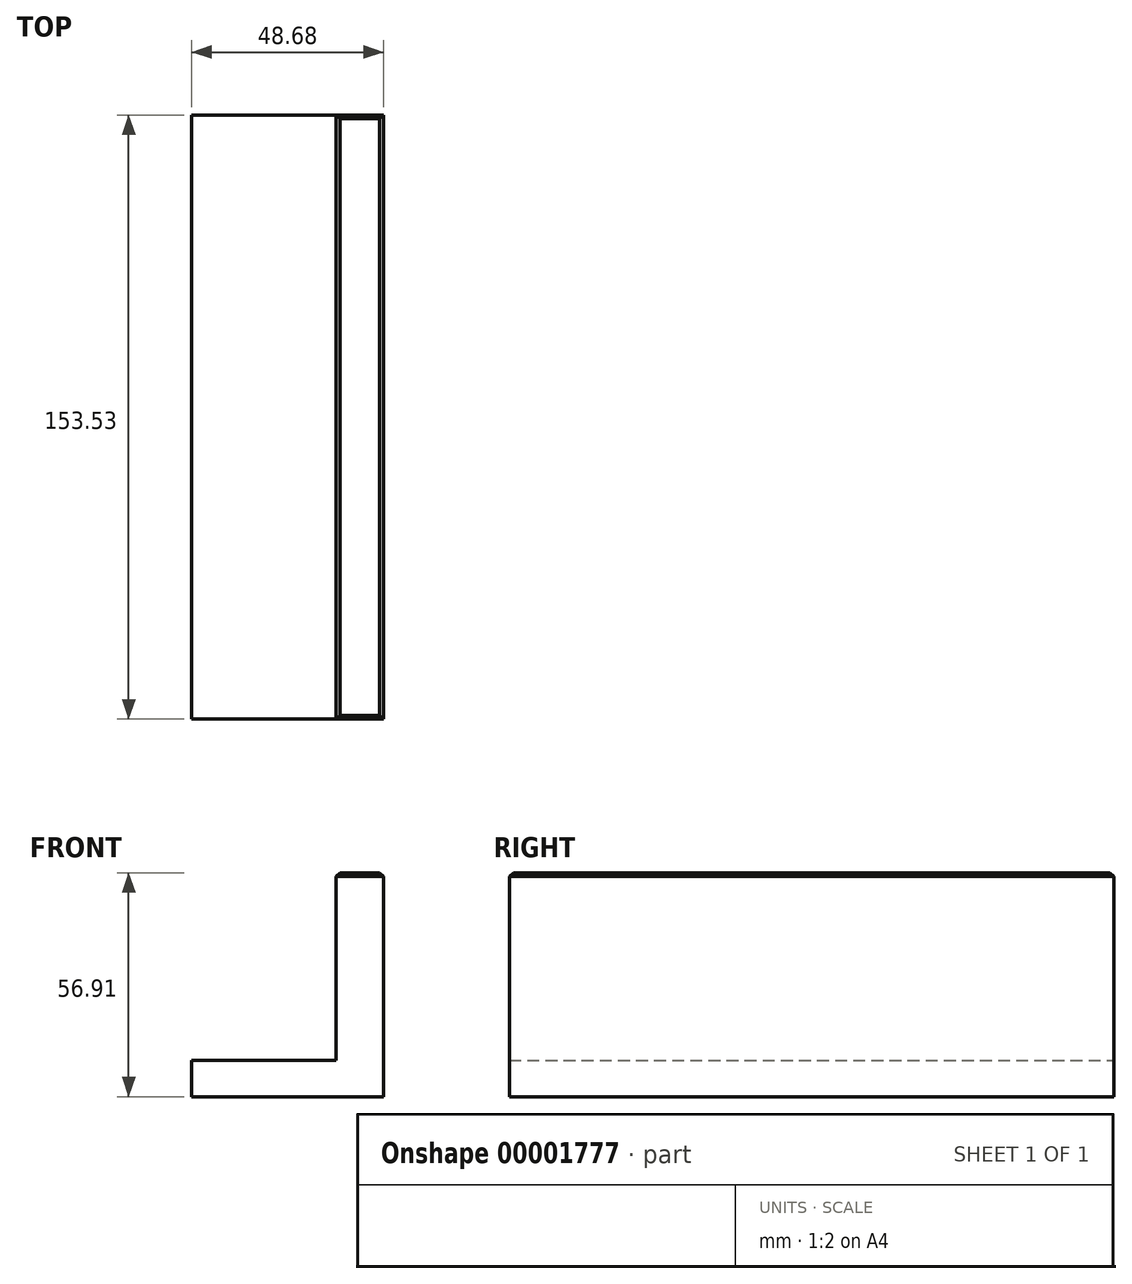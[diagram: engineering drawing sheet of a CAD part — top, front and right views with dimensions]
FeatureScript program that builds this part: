
annotation { "Feature Type Name" : "Feature", "Feature Type Description" : "" }
export const myFeature = defineFeature(function(context is Context, id is Id, definition is map)
    precondition{}
    {
        {
            var Q0;
            Q0=qCreatedBy(makeId("Front.planeOp"),FACE);
            var sketch = newSketch(context, id + "F0", { "sketchPlane" : qUnion([Q0])});
            skLineSegment(sketch, "E0", {"start": v(50.28, 0) * mm, "end": v(0, 0) * mm});
            skLineSegment(sketch, "E1", {"start": v(0, 0) * mm, "end": v(0, 9.18) * mm});
            skLineSegment(sketch, "E2", {"start": v(0, 9.18) * mm, "end": v(36.68, 9.18) * mm});
            skLineSegment(sketch, "E3", {"start": v(36.68, 9.18) * mm, "end": v(36.68, 56.9) * mm});
            skLineSegment(sketch, "E4", {"start": v(36.68, 56.9) * mm, "end": v(48.68, 56.9) * mm});
            skLineSegment(sketch, "E5", {"start": v(48.68, 56.9) * mm, "end": v(48.68, 0) * mm});
            skSolve(sketch);
        }
        {
            var Q0;
            {var subQ0=sQuery(id+"F0.wireOp",EDGE,"E1");Q0=makeQuery(id+"F0.imprint","IMPRINT",FACE,{"disambiguationData":[TD([[makeQuery(id+"F0.imprint","IMPRINT",EDGE,{"derivedFrom":subQ0}),-1.0]])]});}
            extrude(context, id + "F1", {"entities" : qUnion([Q0]), "depth" : 153.53 * mm});
        }
        {
            var Q0;
            Q0=makeQuery(id+"F1.opExtrude","CAP_EDGE",EDGE,{"disambiguationData":[OSD([sQuery(id+"F0.wireOp",EDGE,"E4")])],"isStart":false});
            var Q1;
            Q1=makeQuery(id+"F1.opExtrude","SWEPT_FACE",FACE,{"disambiguationData":[OSD([sQuery(id+"F0.wireOp",EDGE,"E4")])]});
            chamfer(context, id + "F2", {"entities" : qUnion([Q0, Q1]), "width" : 1 * mm, "tangentPropagation" : true});
        }
    });
